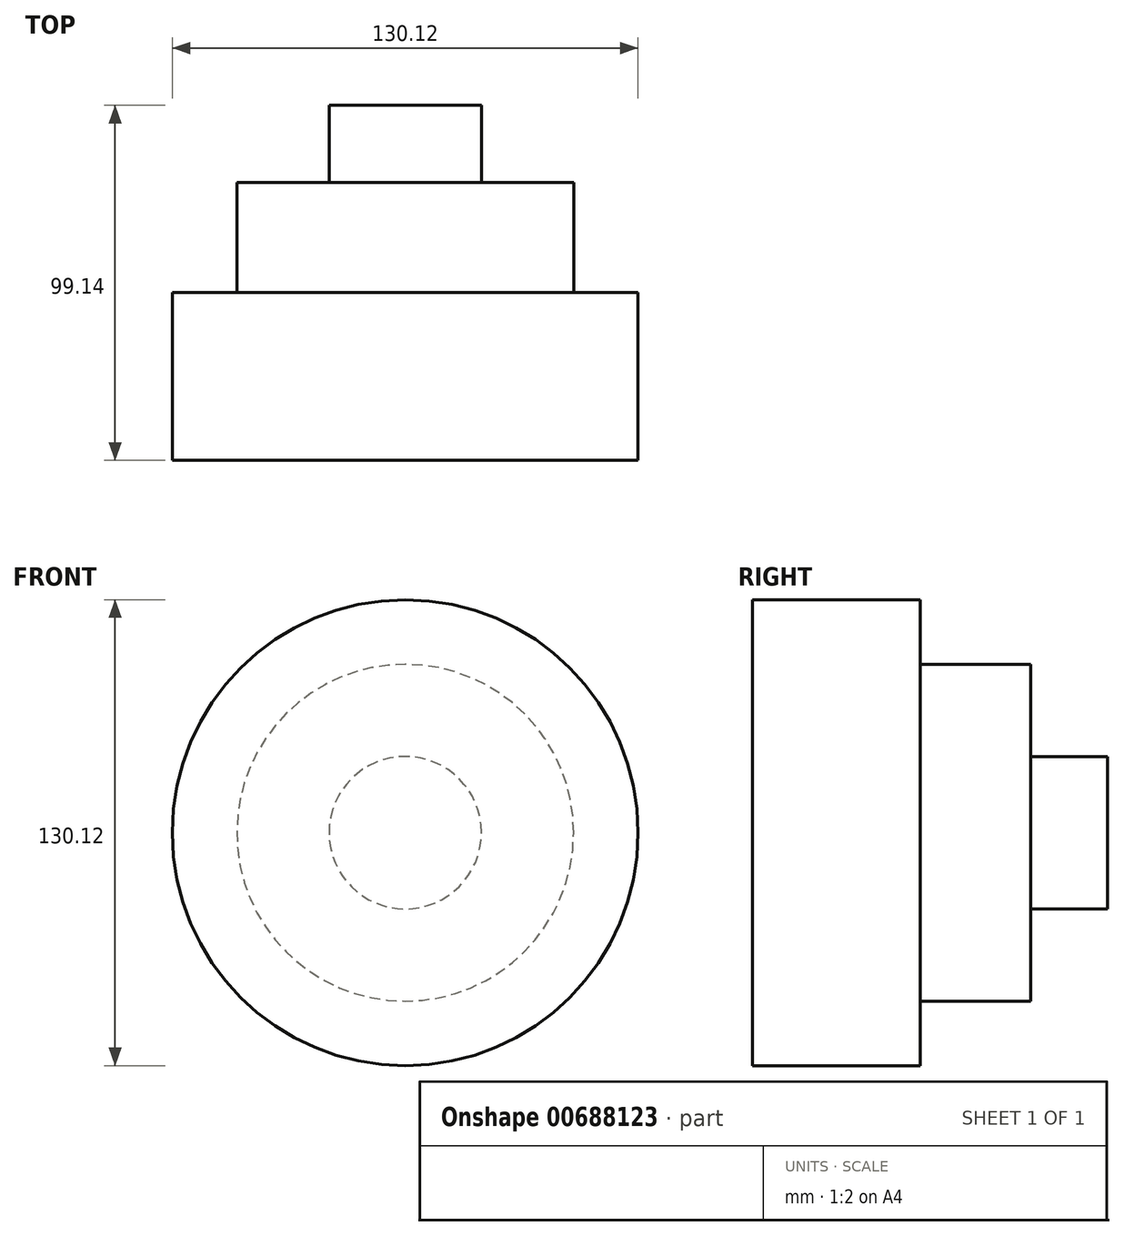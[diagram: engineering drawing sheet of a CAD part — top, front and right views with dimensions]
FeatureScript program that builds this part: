
annotation { "Feature Type Name" : "Feature", "Feature Type Description" : "" }
export const myFeature = defineFeature(function(context is Context, id is Id, definition is map)
    precondition{}
    {
        {
            var Q0;
            Q0=qCreatedBy(makeId("Front.planeOp"),FACE);
            var sketch = newSketch(context, id + "F0", { "sketchPlane" : qUnion([Q0])});
            skCircle(sketch, "E0", {"center": v(0, 0) * mm, "radius": 65.06 * mm});
            skSolve(sketch);
        }
        {
            var Q0;
            Q0=makeQuery(id+"F0.imprint","IMPRINT",FACE,{"disambiguationData":[TD([[makeQuery(id+"F0.imprint","IMPRINT",EDGE,{"derivedFrom":sQuery(id+"F0.wireOp",EDGE,"E0")}),1.0]])]});
            extrude(context, id + "F1", {"entities" : qUnion([Q0]), "oppositeDirection" : true, "depth" : 46.82 * mm, "offsetDistance" : 25.4 * mm});
        }
        {
            var Q0;
            Q0=qCreatedBy(makeId("Front.planeOp"),FACE);
            var sketch = newSketch(context, id + "F2", { "sketchPlane" : qUnion([Q0])});
            skCircle(sketch, "E1", {"center": v(0, 0) * mm, "radius": 47.04 * mm});
            skSolve(sketch);
        }
        {
            var Q0;
            Q0=makeQuery(id+"F2.imprint","IMPRINT",FACE,{"disambiguationData":[TD([[makeQuery(id+"F2.imprint","IMPRINT",EDGE,{"derivedFrom":sQuery(id+"F2.wireOp",EDGE,"E1")}),1.0]])]});
            extrude(context, id + "F3", {"entities" : qUnion([Q0]), "operationType" : NewBodyOperationType.ADD, "oppositeDirection" : true, "depth" : 77.64 * mm, "offsetDistance" : 25.4 * mm});
        }
        {
            var Q0;
            Q0=qCreatedBy(makeId("Front.planeOp"),FACE);
            var sketch = newSketch(context, id + "F4", { "sketchPlane" : qUnion([Q0])});
            skCircle(sketch, "E2", {"center": v(0, 0) * mm, "radius": 21.28 * mm});
            skSolve(sketch);
        }
        {
            var Q0;
            Q0=makeQuery(id+"F4.imprint","IMPRINT",FACE,{"disambiguationData":[TD([[makeQuery(id+"F4.imprint","IMPRINT",EDGE,{"derivedFrom":sQuery(id+"F4.wireOp",EDGE,"E2")}),1.0]])]});
            extrude(context, id + "F5", {"entities" : qUnion([Q0]), "operationType" : NewBodyOperationType.ADD, "oppositeDirection" : true, "depth" : 99.14 * mm, "offsetDistance" : 25.4 * mm});
        }
    });
